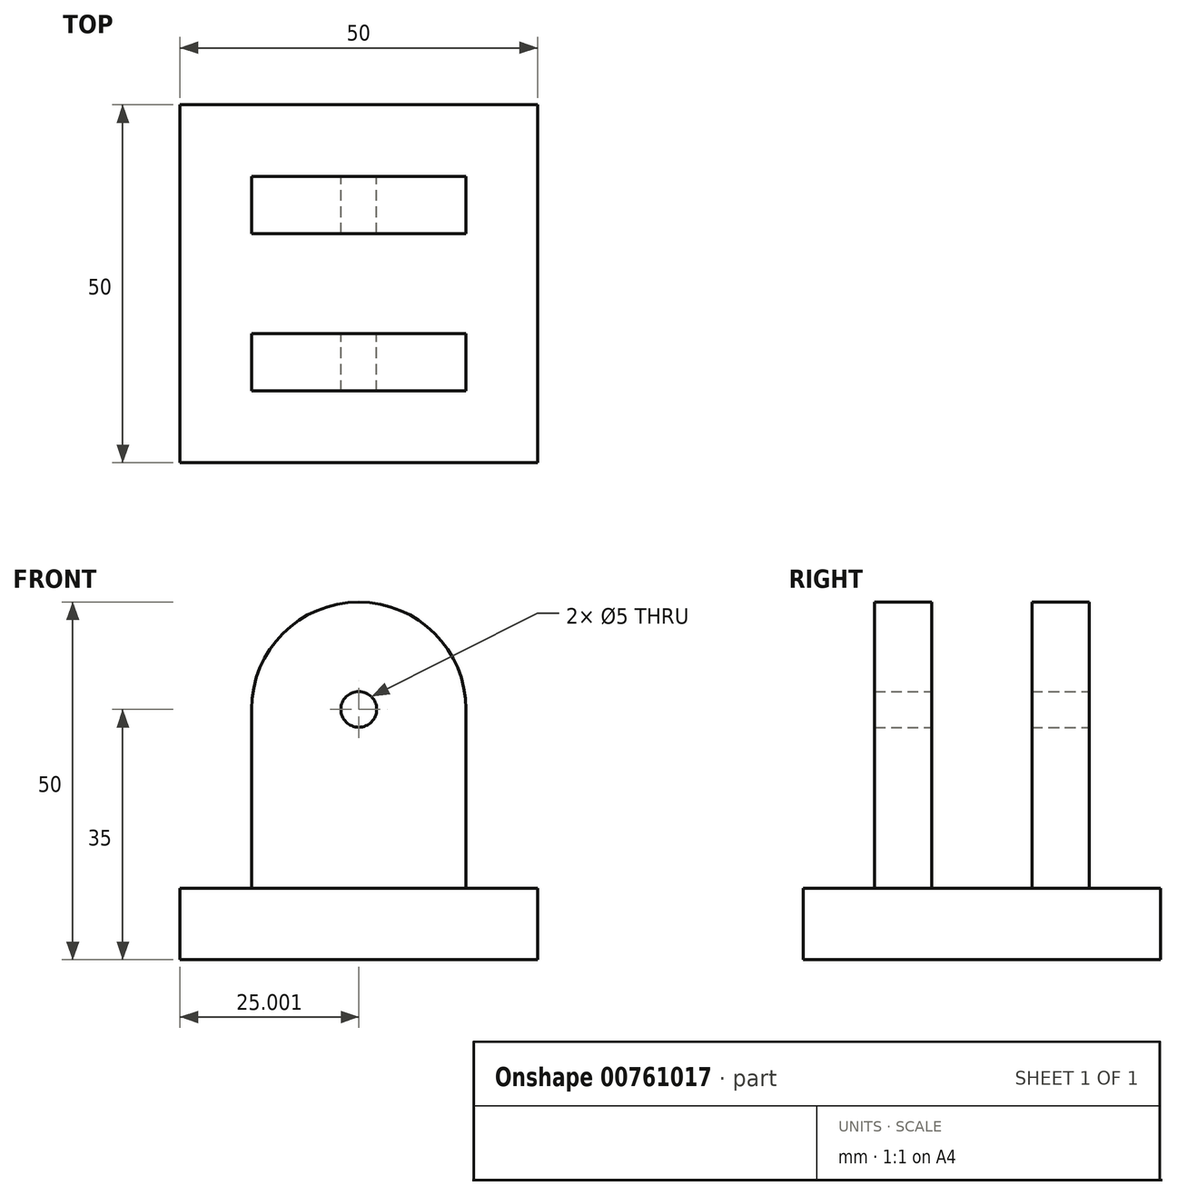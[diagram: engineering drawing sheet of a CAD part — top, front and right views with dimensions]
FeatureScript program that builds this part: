
annotation { "Feature Type Name" : "Feature", "Feature Type Description" : "" }
export const myFeature = defineFeature(function(context is Context, id is Id, definition is map)
    precondition{}
    {
        {
            var Q0;
            Q0=qCreatedBy(makeId("Top.planeOp"),FACE);
            var sketch = newSketch(context, id + "F0", { "sketchPlane" : qUnion([Q0])});
            skLineSegment(sketch, "E0.bottom", {"start": v(-22.95, 22.1) * mm, "end": v(27.05, 22.1) * mm});
            skLineSegment(sketch, "E0.top", {"start": v(-22.95, -27.9) * mm, "end": v(27.05, -27.9) * mm});
            skLineSegment(sketch, "E0.left", {"start": v(-22.95, 22.1) * mm, "end": v(-22.95, -27.9) * mm});
            skLineSegment(sketch, "E0.right", {"start": v(27.05, 22.1) * mm, "end": v(27.05, -27.9) * mm});
            skSolve(sketch);
        }
        {
            var Q0;
            Q0=makeQuery(id+"F0.imprint","IMPRINT",FACE,{"disambiguationData":[TD([[makeQuery(id+"F0.imprint","IMPRINT",EDGE,{"derivedFrom":sQuery(id+"F0.wireOp",EDGE,"E0.bottom")}),-1.0]])]});
            extrude(context, id + "F1", {"entities" : qUnion([Q0]), "depth" : 10 * mm, "offsetDistance" : 25 * mm});
        }
        {
            var Q0;
            Q0=makeQuery(id+"F1.opExtrude","CAP_FACE",FACE,{"disambiguationData":[OSD([sQuery(id+"F0.wireOp",EDGE,"E0.bottom"),sQuery(id+"F0.wireOp",EDGE,"E0.top"),sQuery(id+"F0.wireOp",EDGE,"E0.left"),sQuery(id+"F0.wireOp",EDGE,"E0.right")])],"isStart":false});
            var sketch = newSketch(context, id + "F2", { "sketchPlane" : qUnion([Q0])});
            skLineSegment(sketch, "E1.bottom", {"start": v(-12.95, 12.1) * mm, "end": v(17.05, 12.1) * mm});
            skLineSegment(sketch, "E1.top", {"start": v(-12.95, 4.1) * mm, "end": v(17.05, 4.1) * mm});
            skLineSegment(sketch, "E1.left", {"start": v(-12.95, 12.1) * mm, "end": v(-12.95, 4.1) * mm});
            skLineSegment(sketch, "E1.right", {"start": v(17.05, 12.1) * mm, "end": v(17.05, 4.1) * mm});
            skSolve(sketch);
        }
        {
            var Q0;
            Q0=makeQuery(id+"F2.imprint","IMPRINT",FACE,{"disambiguationData":[TD([[makeQuery(id+"F2.imprint","IMPRINT",EDGE,{"derivedFrom":sQuery(id+"F2.wireOp",EDGE,"E1.bottom")}),1.0]])]});
            var sketch = newSketch(context, id + "F3", { "sketchPlane" : qUnion([Q0])});
            skLineSegment(sketch, "E2.bottom", {"start": v(-12.95, -9.9) * mm, "end": v(17.05, -9.9) * mm});
            skLineSegment(sketch, "E2.top", {"start": v(-12.95, -17.9) * mm, "end": v(17.05, -17.9) * mm});
            skLineSegment(sketch, "E2.left", {"start": v(-12.95, -9.9) * mm, "end": v(-12.95, -17.9) * mm});
            skLineSegment(sketch, "E2.right", {"start": v(17.05, -9.9) * mm, "end": v(17.05, -17.9) * mm});
            skSolve(sketch);
        }
        {
            var Q0;
            Q0=makeQuery(id+"F2.imprint","IMPRINT",FACE,{"disambiguationData":[TD([[makeQuery(id+"F2.imprint","IMPRINT",EDGE,{"derivedFrom":sQuery(id+"F2.wireOp",EDGE,"E1.bottom")}),-1.0]])]});
            extrude(context, id + "F4", {"entities" : qUnion([Q0]), "operationType" : NewBodyOperationType.ADD, "depth" : 40 * mm, "offsetDistance" : 25 * mm});
        }
        {
            var Q0;
            Q0=makeQuery(id+"F3.imprint","IMPRINT",FACE,{"disambiguationData":[TD([[makeQuery(id+"F3.imprint","IMPRINT",EDGE,{"derivedFrom":sQuery(id+"F3.wireOp",EDGE,"E2.bottom")}),-1.0]])]});
            extrude(context, id + "F5", {"entities" : qUnion([Q0]), "operationType" : NewBodyOperationType.ADD, "depth" : 40 * mm, "offsetDistance" : 25 * mm});
        }
        {
            var Q0;
            Q0=makeQuery(id+"F4.opExtrude","CAP_EDGE",EDGE,{"disambiguationData":[OSD([sQuery(id+"F2.wireOp",EDGE,"E1.right")])],"isStart":false});
            fillet(context, id + "F6", {"entities" : qUnion([Q0]), "radius" : 15 * mm, "tangentPropagation" : true, "allowEdgeOverflow" : false});
        }
        {
            var Q0;
            Q0=makeQuery(id+"F5.opExtrude","CAP_EDGE",EDGE,{"disambiguationData":[OSD([sQuery(id+"F3.wireOp",EDGE,"E2.right")])],"isStart":false});
            fillet(context, id + "F7", {"entities" : qUnion([Q0]), "radius" : 15 * mm, "tangentPropagation" : true, "allowEdgeOverflow" : false});
        }
        {
            var Q0;
            Q0=makeQuery(id+"F4.opExtrude","CAP_EDGE",EDGE,{"disambiguationData":[OSD([sQuery(id+"F2.wireOp",EDGE,"E1.left")])],"isStart":false});
            fillet(context, id + "F8", {"entities" : qUnion([Q0]), "radius" : 15 * mm, "tangentPropagation" : true, "allowEdgeOverflow" : false});
        }
        {
            var Q0;
            Q0=makeQuery(id+"F5.opExtrude","CAP_EDGE",EDGE,{"disambiguationData":[OSD([sQuery(id+"F3.wireOp",EDGE,"E2.left")])],"isStart":false});
            fillet(context, id + "F9", {"entities" : qUnion([Q0]), "radius" : 15 * mm, "tangentPropagation" : true, "allowEdgeOverflow" : false});
        }
        {
            var Q0;
            Q0=makeQuery(id+"F4.opExtrude","SWEPT_FACE",FACE,{"disambiguationData":[OSD([sQuery(id+"F2.wireOp",EDGE,"E1.bottom")])]});
            var sketch = newSketch(context, id + "F10", { "sketchPlane" : qUnion([Q0])});
            skCircle(sketch, "E3", {"center": v(-2.05, 35) * mm, "radius": 2.5 * mm});
            skSolve(sketch);
        }
        {
            var Q0;
            Q0=sQuery(id+"F10.wireOp",VERTEX,"E3.center");
            var Q1;
            Q1=makeQuery(id+"F1.opExtrude","SWEPT_BODY",BODY,{"disambiguationData":[OSD([sQuery(id+"F0.wireOp",EDGE,"E0.bottom"),sQuery(id+"F0.wireOp",EDGE,"E0.top"),sQuery(id+"F0.wireOp",EDGE,"E0.left"),sQuery(id+"F0.wireOp",EDGE,"E0.right")])]});
            hole(context, id + "F11", {"style" : HoleStyle.SIMPLE, "endStyle" : HoleEndStyle.THROUGH, "holeDiameter" : 5 * mm, "majorDiameter" : 5 * mm, "isTappedThrough" : true, "tappedDepth" : 12 * mm, "tapClearance" : 3, "locations" : qUnion([Q0]), "scope" : qUnion([Q1])});
        }
    });
